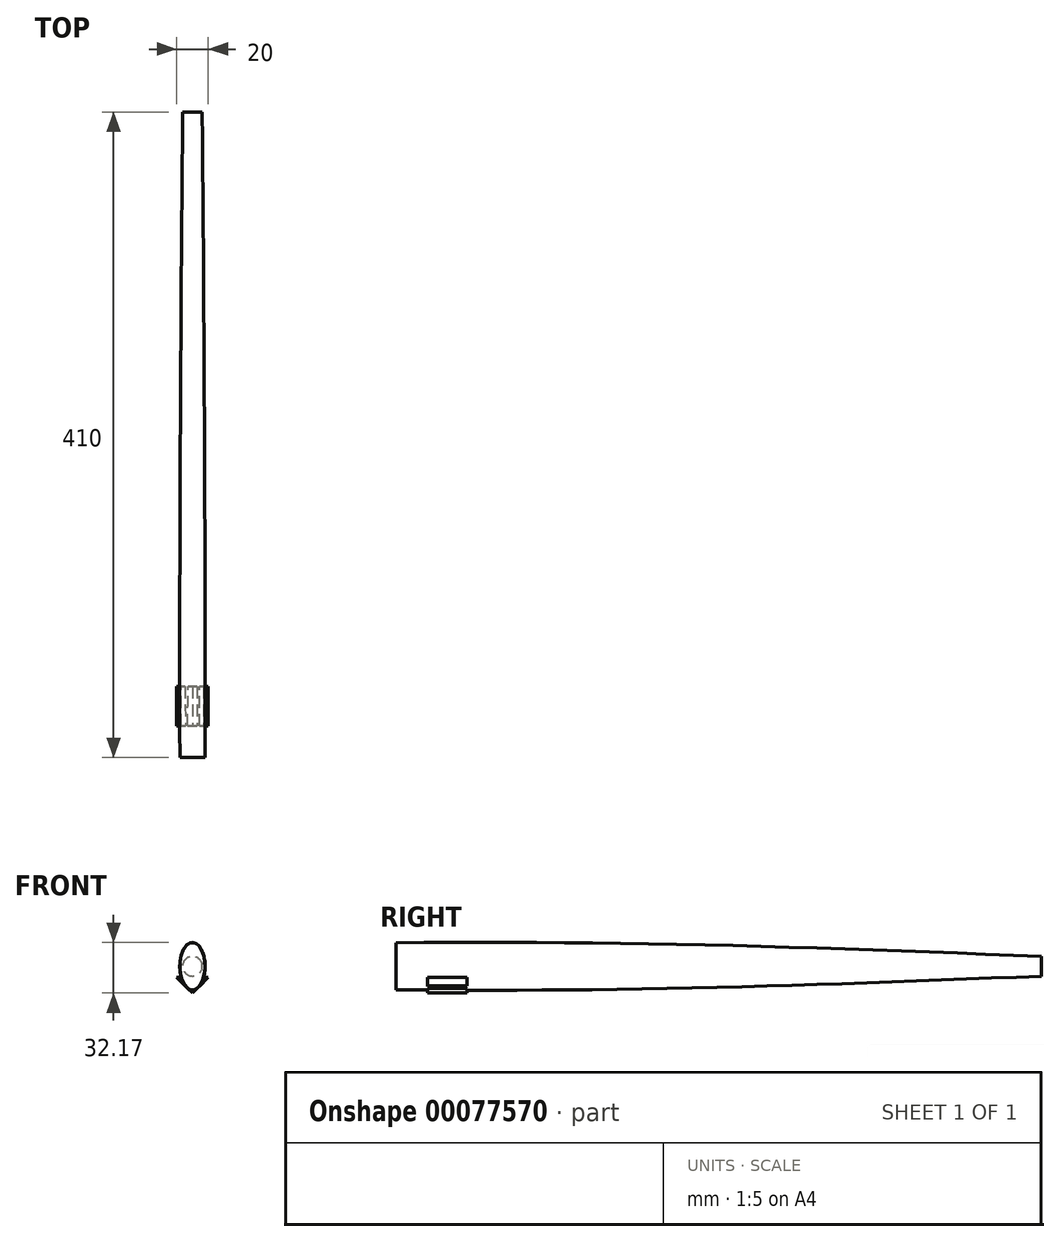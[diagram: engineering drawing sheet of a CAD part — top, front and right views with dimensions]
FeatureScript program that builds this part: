
annotation { "Feature Type Name" : "Feature", "Feature Type Description" : "" }
export const myFeature = defineFeature(function(context is Context, id is Id, definition is map)
    precondition{}
    {
        {
            var Q0;
            Q0=qCreatedBy(makeId("Front.planeOp"),FACE);
            var sketch = newSketch(context, id + "F0", { "sketchPlane" : qUnion([Q0])});
            skEllipse(sketch, "E0", {"center": v(0, 0) * mm, "majorRadius": 15 * mm, "minorRadius": 8 * mm, "majorAxis": v(0, 1)});
            skSolve(sketch);
        }
        {
            var Q0;
            Q0=qCreatedBy(makeId("Front.planeOp"),FACE);
            cPlane(context, id + "F1", {"entities" : qUnion([Q0]), "cplaneType" : CPlaneType.OFFSET, "offset" : 110 * mm, "oppositeDirection" : true, "width" : 150 * mm, "height" : 150 * mm});
        }
        {
            var Q0;
            Q0=qCreatedBy(id+"F1.planeOp",FACE);
            cPlane(context, id + "F2", {"entities" : qUnion([Q0]), "cplaneType" : CPlaneType.OFFSET, "offset" : 300 * mm, "oppositeDirection" : true, "width" : 150 * mm, "height" : 150 * mm});
        }
        {
            var Q0;
            Q0=qCreatedBy(id+"F1.planeOp",FACE);
            var sketch = newSketch(context, id + "F3", { "sketchPlane" : qUnion([Q0])});
            skEllipse(sketch, "E1", {"center": v(0, 0) * mm, "majorRadius": 15 * mm, "minorRadius": 8 * mm, "majorAxis": v(0, 1)});
            skSolve(sketch);
        }
        {
            var Q0;
            Q0=qCreatedBy(id+"F2.planeOp",FACE);
            var sketch = newSketch(context, id + "F4", { "sketchPlane" : qUnion([Q0])});
            skCircle(sketch, "E2", {"center": v(0, 0) * mm, "radius": 6.25 * mm});
            skSolve(sketch);
        }
        {
            var Q0;
            Q0=makeQuery(id+"F0.imprint","IMPRINT",FACE,{"disambiguationData":[TD([[makeQuery(id+"F0.imprint","IMPRINT",EDGE,{"derivedFrom":sQuery(id+"F0.wireOp",EDGE,"E0")}),1.0]])]});
            var Q1;
            Q1=makeQuery(id+"F3.imprint","IMPRINT",FACE,{"disambiguationData":[TD([[makeQuery(id+"F3.imprint","IMPRINT",EDGE,{"derivedFrom":sQuery(id+"F3.wireOp",EDGE,"E1")}),1.0]])]});
            var Q2;
            Q2=makeQuery(id+"F4.imprint","IMPRINT",FACE,{"disambiguationData":[TD([[makeQuery(id+"F4.imprint","IMPRINT",EDGE,{"derivedFrom":sQuery(id+"F4.wireOp",EDGE,"E2")}),1.0]])]});
            loft(context, id + "F5", {"sheetProfilesArray" : [{ "sheetProfileEntities" : qUnion([Q0]) }, { "sheetProfileEntities" : qUnion([Q1]) }, { "sheetProfileEntities" : qUnion([Q2]) }]});
        }
        {
            var Q0;
            Q0=qCreatedBy(makeId("Front.planeOp"),FACE);
            cPlane(context, id + "F6", {"entities" : qUnion([Q0]), "cplaneType" : CPlaneType.OFFSET, "offset" : 20 * mm, "oppositeDirection" : true, "width" : 150 * mm, "height" : 150 * mm});
        }
        {
            var Q0;
            Q0=qCreatedBy(id+"F6.planeOp",FACE);
            var sketch = newSketch(context, id + "F7", { "sketchPlane" : qUnion([Q0])});
            skLineSegment(sketch, "E3", {"start": v(-10, -7) * mm, "end": v(0, -17) * mm});
            skLineSegment(sketch, "E4", {"start": v(0, -17) * mm, "end": v(10, -7) * mm});
            skLineSegment(sketch, "E5", {"start": v(10, -7) * mm, "end": v(-10, -7) * mm});
            skSolve(sketch);
        }
        {
            var Q0;
            Q0 = qSketchRegion(id + "F7", true);
            extrude(context, id + "F8", {"entities" : qUnion([Q0]), "operationType" : NewBodyOperationType.ADD, "oppositeDirection" : true, "depth" : 25 * mm});
        }
    });
